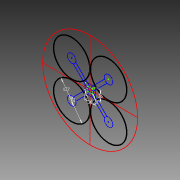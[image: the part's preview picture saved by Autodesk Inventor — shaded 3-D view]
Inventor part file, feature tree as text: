
AUTODESK INVENTOR PART (.ipt)
format: ipt  version: 2015 (Build 190159000, 159)  size: 86,016 bytes
history: native  units: mm
features: sketch x1
ambient origin geometry x8: Origin, YZ Plane, XZ Plane, XY Plane, X Axis, Y Axis, Z Axis, Center Point
feature tree (1):
  sketch  "Sketch1"  dims[d0=36.0mm d1=36.0mm d13=12.0mm d16=30.0mm d18=127.0mm d41=3.0mm d43=3.0mm]
